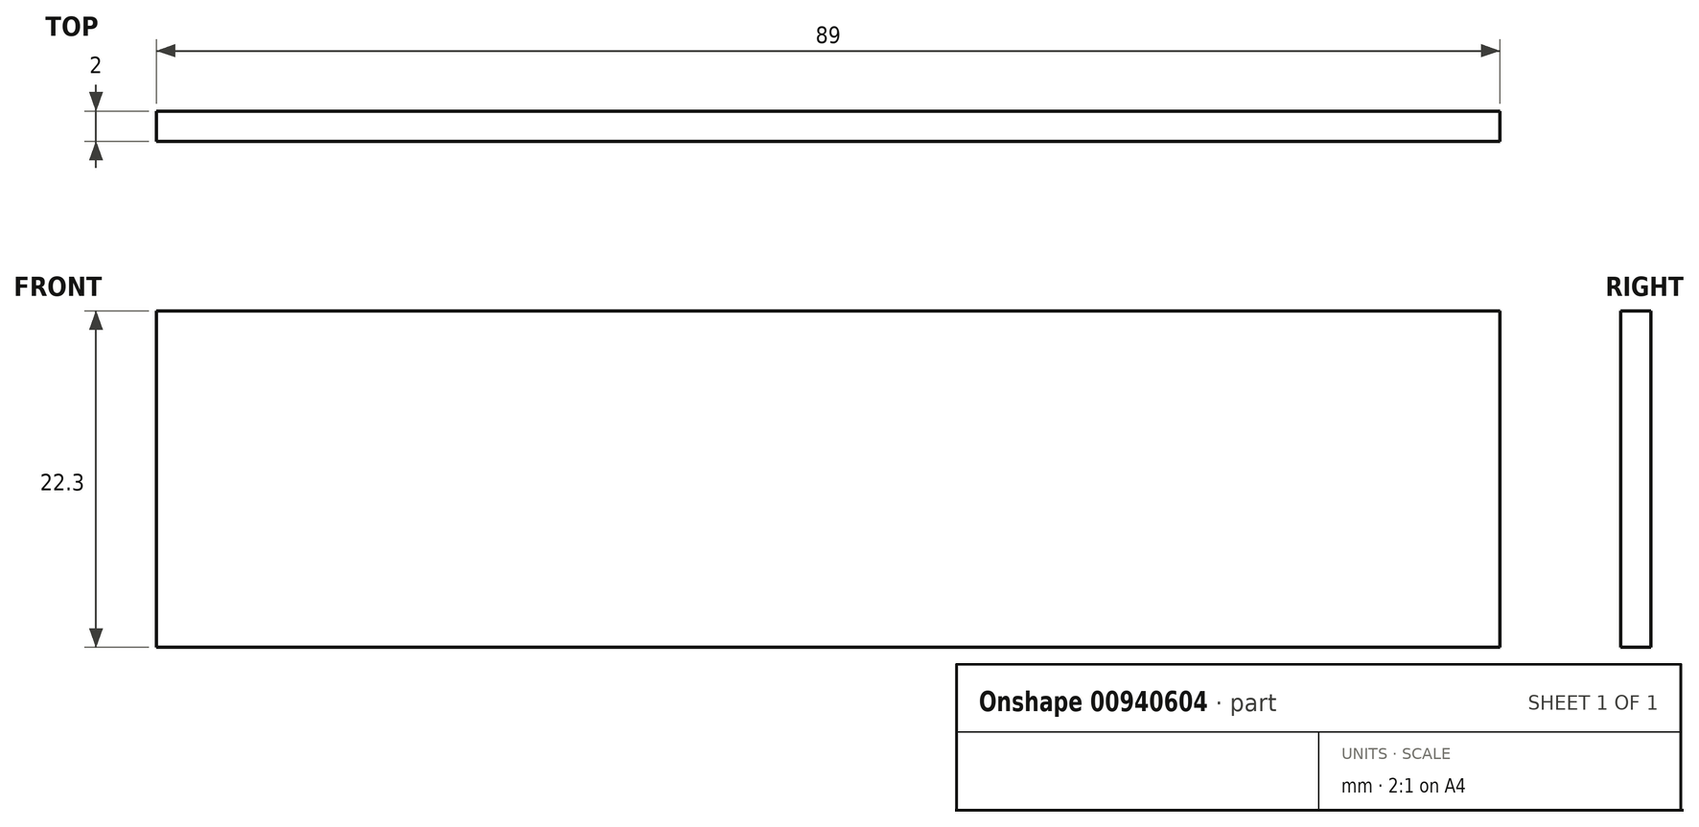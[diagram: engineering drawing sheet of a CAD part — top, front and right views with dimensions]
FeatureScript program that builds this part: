
annotation { "Feature Type Name" : "Feature", "Feature Type Description" : "" }
export const myFeature = defineFeature(function(context is Context, id is Id, definition is map)
    precondition{}
    {
        {
            var Q0;
            Q0=qCreatedBy(makeId("Front.planeOp"),FACE);
            var sketch = newSketch(context, id + "F0", { "sketchPlane" : qUnion([Q0])});
            skLineSegment(sketch, "E0.bottom", {"start": v(-44.5, 9.12) * mm, "end": v(44.5, 9.12) * mm});
            skLineSegment(sketch, "E0.top", {"start": v(-44.5, -13.18) * mm, "end": v(44.5, -13.18) * mm});
            skLineSegment(sketch, "E0.left", {"start": v(-44.5, 9.12) * mm, "end": v(-44.5, -13.18) * mm});
            skLineSegment(sketch, "E0.right", {"start": v(44.5, 9.12) * mm, "end": v(44.5, -13.18) * mm});
            skSolve(sketch);
        }
        {
            var Q0;
            Q0 = qSketchRegion(id + "F0", true);
            extrude(context, id + "F1", {"entities" : qUnion([Q0]), "depth" : 2 * mm, "offsetDistance" : 25.4 * mm});
        }
    });
